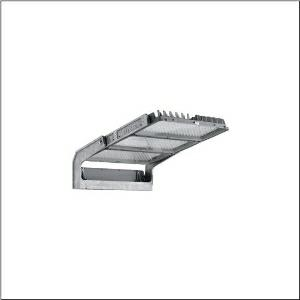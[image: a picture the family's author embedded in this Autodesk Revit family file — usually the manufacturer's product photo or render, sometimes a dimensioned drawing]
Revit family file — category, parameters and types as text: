
# Revit family: floodlight_fl_11_maxi_pro___rs12_5xa779228m01ab_5605
name_source: partatom
category: Lighting Fixtures
units: mm (PartAtom-declared; Revit-internal decimal feet)

## family parameters
Cut with Voids When Loaded = No
Host = Face
Light Source = No
Part Type = Normal
Room Calculation Point = No
Round Connector Dimension = Use Diameter
Shared = No

## types (1)
- --- (1 x LED, 179630 lm, 1571.1 W, 5700K)
    Apparent Load = 1571 VA
    CIE Flux Codes = 79 92 99 100 100
    Color Rendering = 80
    Color Temperature = 5700K
    Default Elevation = 1800 mm
    Description = Floodlight FL 11  maxi  pro floodlight; light control with lens of PMMA; cover panel of toughened safety glass, transparent; light distribution: RS12, rotationally symmetric direct distribution, LED; colour temperature: 5700K, rated luminous flux: 179.630lm, colour rendering: CRI > 80, light colour: 857; luminous efficacy: 114lm/W; brightness control: DMX+RDM; with terminal, 6-pole, max. 2.5mm², mains connection: 220..240V/380..400V AC, 50/60Hz, surge voltage resistance: line to ground: 10kV, service life up to 100,000h L90. Typical operating time: 1000h per year, ECG replaceable separately, LED unit replaceable without ESD environment, dustproof LED module, dimming range 10..100%; 1571W floodlight with 3x LED unit of diecast aluminium, coated grey; length: 1.003mm / width: 651mm / height: 338mm; mounting bracket, of diecast aluminium, uncoated, natural, equipment: Power, protection rating (complete): IP66; insulation class (complete): insulation class I (protective earthing); certification: CE, ENEC, VDE; ball protection: ball impact resistant, only for outdoor installations in the designated locations, permissible operating ambient temperature: -40..+55°C, permissible storage temperature: -40..+85°Cpackaging unit: 1 piece

Light Distribution: RS12
    Height = 320 mm
    Lamp = 1 x LED
    Lamp Light Flux = 179630 lm
    Lamp Power = 1571.1 W
    Lamp count = 1
    Length = 1002 mm
    Luminous efficacy = 114 lm/W
    Manufacturer = Siteco
    ModVariant = No
    Model = 5XA779228M01AB
    Mounting Place = Ceiling
    Mounting Type = Surface mounted
    Number of Poles = 1
    OnlyDefault = Yes
    Power Factor = 1
    Product Name = Floodlight FL 11 maxi pro | RS12
    Product group = floodlight | ceiling mounted
    ProductGroupID = 302
    Protection Class = Protection class I
    Protection Degree = IP 66
    RLX_Detail_Level = 1
    RLX_Emergency_Light_Flux = 0 lm
    RLX_Emergency_Type = 0
    RLX_Emergency_Type_DB = No
    RlxData = <blob elided: 40441 chars, md5=1a1f6e73>
    Socket = socket
    Standby Power = 0 W
    System Light Flux = 179630 lm
    System Power = 1571 W
    Type Comments = factory setting: luminous flux: 100 % | dim-lin: 255 | 1060 mA
    Type Image = l_1356210.jpg
    URL = http://relux.com
    VarID = @adj_034007
    Voltage = 0 V
    Weight = 0.00 kg
    Width = 655 mm

## geometry (parser evidence)
native form markers: Blend x4, Sweep x14
no freeform markers — native parametric forms only
